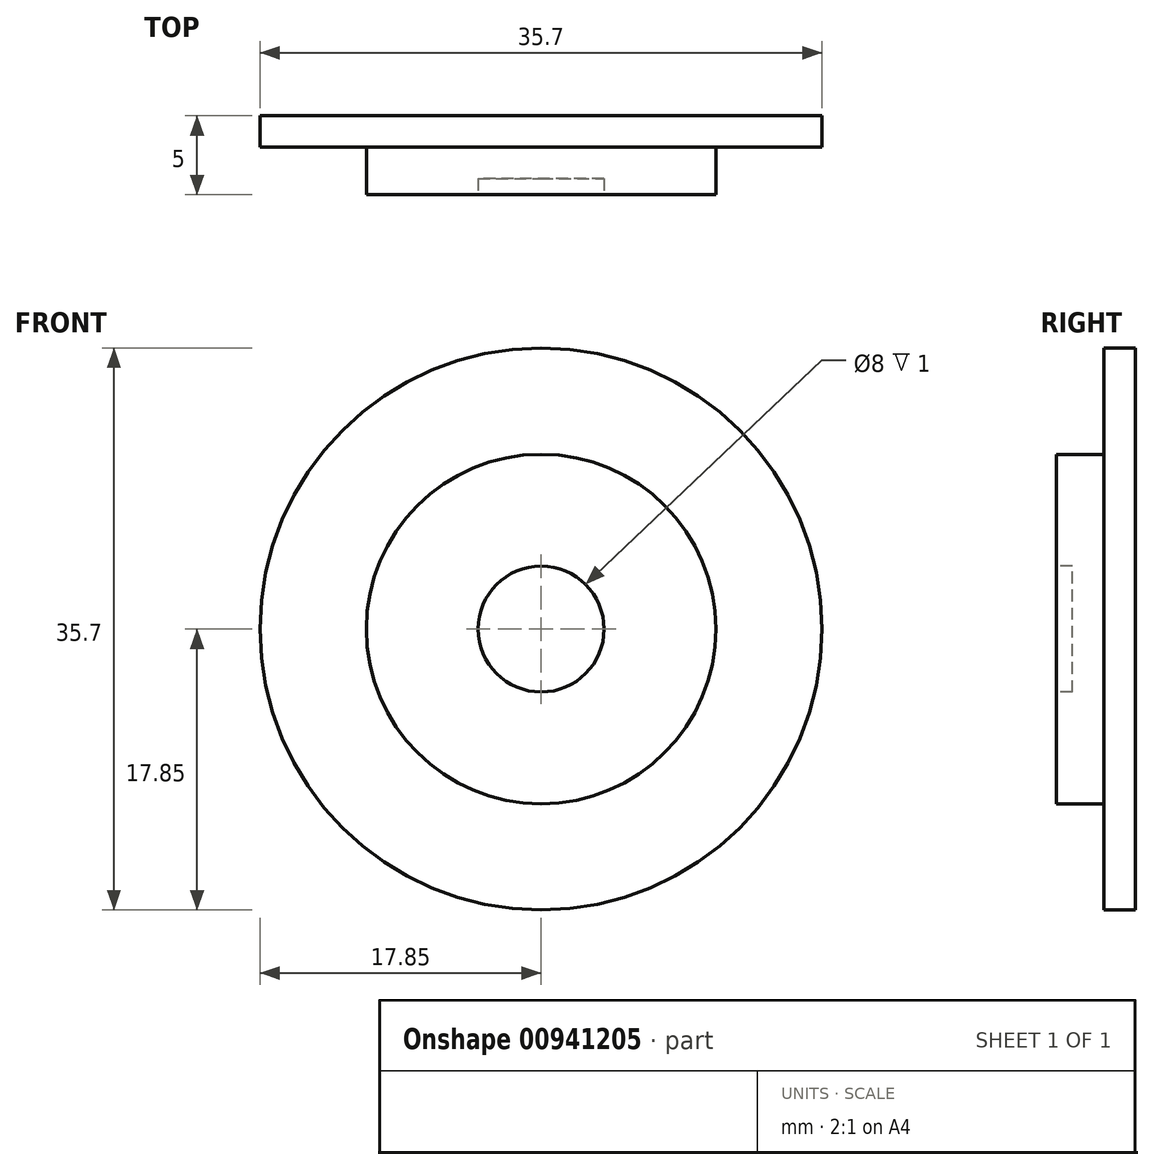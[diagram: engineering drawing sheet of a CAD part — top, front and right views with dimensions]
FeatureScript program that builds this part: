
annotation { "Feature Type Name" : "Feature", "Feature Type Description" : "" }
export const myFeature = defineFeature(function(context is Context, id is Id, definition is map)
    precondition{}
    {
        {
            var Q0;
            Q0=qCreatedBy(makeId("Front.planeOp"),FACE);
            var sketch = newSketch(context, id + "F0", { "sketchPlane" : qUnion([Q0])});
            skCircle(sketch, "E0", {"center": v(0, 0) * mm, "radius": 11.1 * mm});
            skCircle(sketch, "E1", {"center": v(0, 0) * mm, "radius": 17.85 * mm});
            skSolve(sketch);
        }
        {
            var Q0;
            Q0=makeQuery(id+"F0.imprint","IMPRINT",FACE,{"disambiguationData":[TD([[makeQuery(id+"F0.imprint","IMPRINT",EDGE,{"derivedFrom":sQuery(id+"F0.wireOp",EDGE,"E0")}),1.0]])]});
            var Q1;
            Q1=makeQuery(id+"F0.imprint","IMPRINT",FACE,{"disambiguationData":[TD([[makeQuery(id+"F0.imprint","IMPRINT",EDGE,{"derivedFrom":sQuery(id+"F0.wireOp",EDGE,"E0")}),-1.0]])]});
            extrude(context, id + "F1", {"entities" : qUnion([Q0, Q1]), "depth" : 2 * mm, "offsetDistance" : 25 * mm});
        }
        {
            var Q0;
            Q0=makeQuery(id+"F0.imprint","IMPRINT",FACE,{"disambiguationData":[TD([[makeQuery(id+"F0.imprint","IMPRINT",EDGE,{"derivedFrom":sQuery(id+"F0.wireOp",EDGE,"E0")}),1.0]])]});
            extrude(context, id + "F2", {"entities" : qUnion([Q0]), "operationType" : NewBodyOperationType.ADD, "depth" : 5 * mm, "offsetDistance" : 25 * mm});
        }
        {
            var Q0;
            Q0=makeQuery(id+"F2.opExtrude","CAP_FACE",FACE,{"disambiguationData":[OSD([sQuery(id+"F0.wireOp",EDGE,"E0")])],"isStart":false});
            var sketch = newSketch(context, id + "F3", { "sketchPlane" : qUnion([Q0])});
            skCircle(sketch, "E2", {"center": v(0, 0) * mm, "radius": 4 * mm});
            skSolve(sketch);
        }
        {
            var Q0;
            Q0=makeQuery(id+"F3.imprint","IMPRINT",FACE,{"disambiguationData":[TD([[makeQuery(id+"F3.imprint","IMPRINT",EDGE,{"derivedFrom":sQuery(id+"F3.wireOp",EDGE,"E2")}),1.0]])]});
            extrude(context, id + "F4", {"entities" : qUnion([Q0]), "operationType" : NewBodyOperationType.REMOVE, "oppositeDirection" : true, "depth" : 1 * mm, "offsetDistance" : 25 * mm});
        }
    });
